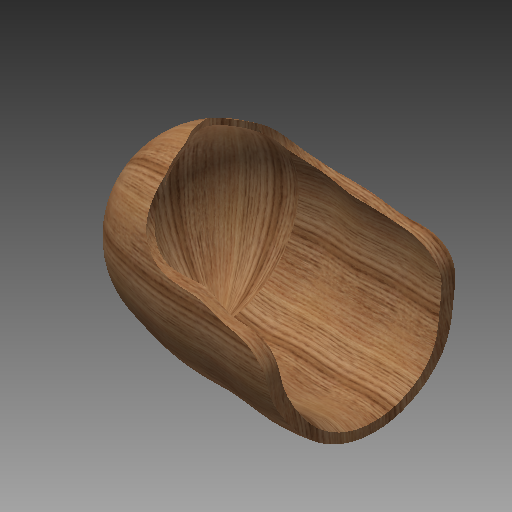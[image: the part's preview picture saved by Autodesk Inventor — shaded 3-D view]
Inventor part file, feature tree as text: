
AUTODESK INVENTOR PART (.ipt)
format: ipt  version: 2022 (Build 260153000, 153)  size: 525,824 bytes
history: native  units: mm (DEFAULTED — no unit token found)
features: sketch x2, other x1, revolve x1, extrude x1
ambient origin geometry x8: Origin, YZ Plane, XZ Plane, XY Plane, X Axis, Y Axis, Z Axis, Center Point
bodies: Body1 (feature_tree)
feature tree (5):
  other  "iMandy - 2D BODY"
  revolve  "Revolution2"  [1 undecoded]
  extrude  "Extrusion5"  Depth=152.4mm TaperAngle=0.0deg
  sketch  "Sketch8"  dims[d1=10.0mm d40=92.345631mm d41=167.853868mm]
  sketch  "Sketch9"  dims[d42=90.0deg d43=152.4mm d44=0.0mm d45=139.7mm d47=190.5mm d49=139.7mm d51=15.24mm d52=6.35mm d54=13.97mm d55=0.698132mm d56=7.62mm d57=6.35mm d58=1.524mm d59=2.54mm d60=3.556mm d61=8.89mm d62=10.668mm d63=10.16mm d64=12.7mm d65=10.16mm d66=208.28mm d67=17.78mm d68=33.244427mm d70=55.88mm d71=25.4mm d72=0.0mm d80=47.256954mm d87=8.89mm d89=63.5mm d90=11.170107mm]
note: 1 required parameter value undecoded (feature->parameter linkage not recoverable at this tier; creation-order binding heuristic only, values carry confidence <= 0.55)
